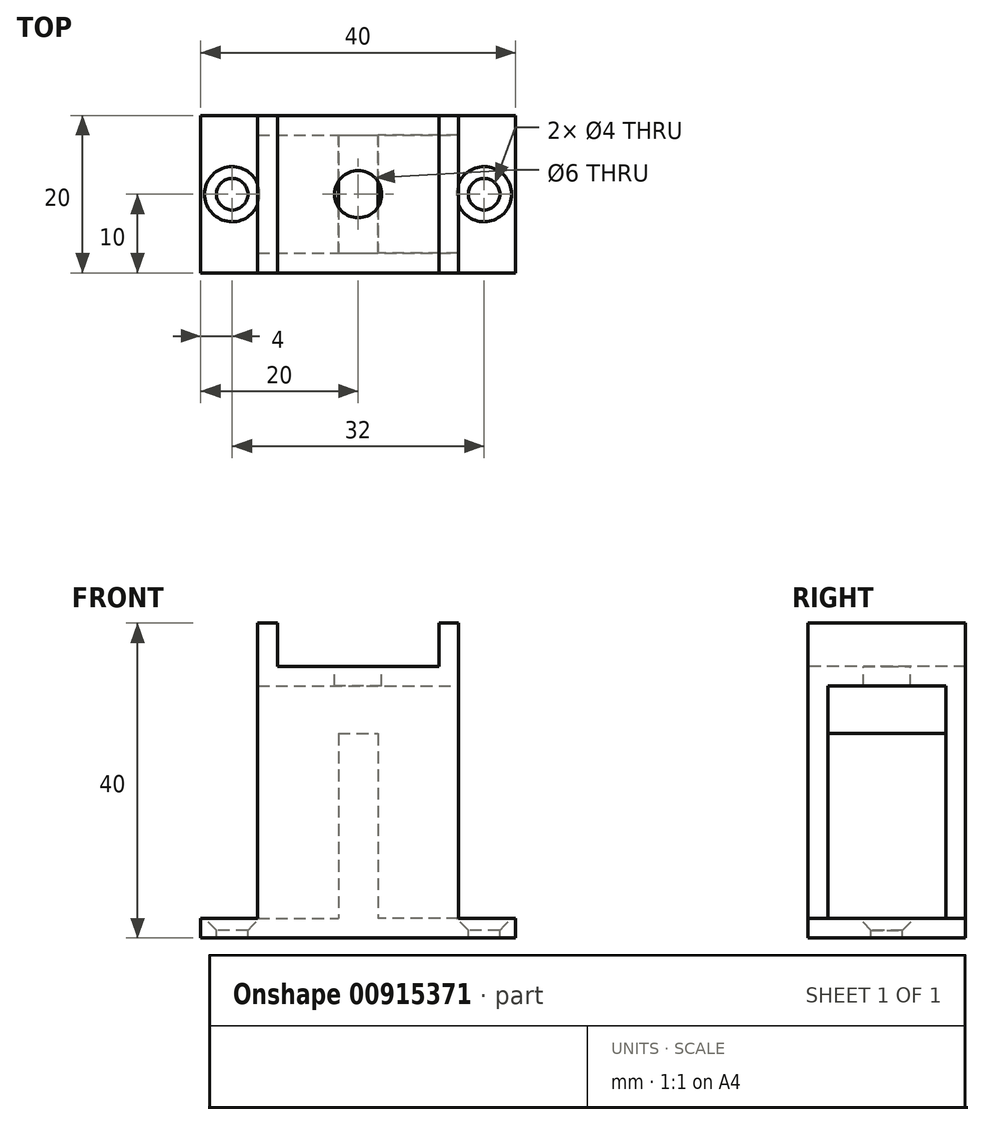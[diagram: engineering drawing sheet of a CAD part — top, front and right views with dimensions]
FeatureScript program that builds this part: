
annotation { "Feature Type Name" : "Feature", "Feature Type Description" : "" }
export const myFeature = defineFeature(function(context is Context, id is Id, definition is map)
    precondition{}
    {
        {
            var Q0;
            Q0=qCreatedBy(makeId("Top.planeOp"),FACE);
            var sketch = newSketch(context, id + "F0", { "sketchPlane" : qUnion([Q0])});
            skLineSegment(sketch, "E0.bottom", {"start": v(-20, 10) * mm, "end": v(20, 10) * mm});
            skLineSegment(sketch, "E0.top", {"start": v(-20, -10) * mm, "end": v(20, -10) * mm});
            skLineSegment(sketch, "E0.left", {"start": v(-20, 10) * mm, "end": v(-20, -10) * mm});
            skLineSegment(sketch, "E0.right", {"start": v(20, 10) * mm, "end": v(20, -10) * mm});
            skSolve(sketch);
        }
        {
            var Q0;
            Q0=makeQuery(id+"F0.imprint","IMPRINT",FACE,{"disambiguationData":[TD([[makeQuery(id+"F0.imprint","IMPRINT",EDGE,{"derivedFrom":sQuery(id+"F0.wireOp",EDGE,"E0.bottom")}),-1.0]])]});
            extrude(context, id + "F1", {"entities" : qUnion([Q0]), "depth" : 40 * mm, "offsetDistance" : 25 * mm});
        }
        {
            var Q0;
            Q0=qCreatedBy(makeId("Top.planeOp"),FACE);
            var sketch = newSketch(context, id + "F2", { "sketchPlane" : qUnion([Q0])});
            skLineSegment(sketch, "E1.bottom", {"start": v(-20, 7.5) * mm, "end": v(-2.5, 7.5) * mm});
            skLineSegment(sketch, "E1.top", {"start": v(-20, -7.5) * mm, "end": v(-2.5, -7.5) * mm});
            skLineSegment(sketch, "E1.left", {"start": v(-20, 7.5) * mm, "end": v(-20, -7.5) * mm});
            skLineSegment(sketch, "E1.right", {"start": v(-2.5, 7.5) * mm, "end": v(-2.5, -7.5) * mm});
            skLineSegment(sketch, "E2.MirrorCS", {"start": v(20, 7.5) * mm, "end": v(2.5, 7.5) * mm});
            skLineSegment(sketch, "E3.MirrorCS", {"start": v(2.5, 7.5) * mm, "end": v(2.5, -7.5) * mm});
            skLineSegment(sketch, "E4.MirrorCS", {"start": v(20, -7.5) * mm, "end": v(2.5, -7.5) * mm});
            skLineSegment(sketch, "E5.MirrorCS", {"start": v(20, 7.5) * mm, "end": v(20, -7.5) * mm});
            skSolve(sketch);
        }
        {
            var Q0;
            Q0 = qSketchRegion(id + "F2", true);
            extrude(context, id + "F3", {"entities" : qUnion([Q0]), "operationType" : NewBodyOperationType.REMOVE, "depth" : 32 * mm, "offsetDistance" : 25 * mm, "hasSecondDirection" : true, "secondDirectionOppositeDirection" : false, "secondDirectionDepth" : 2.5 * mm});
        }
        {
            var Q0;
            Q0=qCreatedBy(makeId("Front.planeOp"),FACE);
            var sketch = newSketch(context, id + "F4", { "sketchPlane" : qUnion([Q0])});
            skLineSegment(sketch, "E6.bottom", {"start": v(-10.25, 40) * mm, "end": v(10.25, 40) * mm});
            skLineSegment(sketch, "E6.top", {"start": v(-10.25, 34.5) * mm, "end": v(10.25, 34.5) * mm});
            skLineSegment(sketch, "E6.left", {"start": v(-10.25, 40) * mm, "end": v(-10.25, 34.5) * mm});
            skLineSegment(sketch, "E6.right", {"start": v(10.25, 40) * mm, "end": v(10.25, 34.5) * mm});
            skLineSegment(sketch, "E7.bottom", {"start": v(-20, 40) * mm, "end": v(-12.75, 40) * mm});
            skLineSegment(sketch, "E7.top", {"start": v(-20, 2.5) * mm, "end": v(-12.75, 2.5) * mm});
            skLineSegment(sketch, "E7.left", {"start": v(-20, 40) * mm, "end": v(-20, 2.5) * mm});
            skLineSegment(sketch, "E7.right", {"start": v(-12.75, 40) * mm, "end": v(-12.75, 2.5) * mm});
            skLineSegment(sketch, "E8.MirrorCS", {"start": v(12.75, 40) * mm, "end": v(12.75, 2.5) * mm});
            skLineSegment(sketch, "E9.MirrorCS", {"start": v(20, 40) * mm, "end": v(12.75, 40) * mm});
            skLineSegment(sketch, "E10.MirrorCS", {"start": v(20, 40) * mm, "end": v(20, 2.5) * mm});
            skLineSegment(sketch, "E11.MirrorCS", {"start": v(20, 2.5) * mm, "end": v(12.75, 2.5) * mm});
            skSolve(sketch);
        }
        {
            var Q0;
            Q0 = qSketchRegion(id + "F4", true);
            extrude(context, id + "F5", {"entities" : qUnion([Q0]), "operationType" : NewBodyOperationType.REMOVE, "oppositeDirection" : true, "depth" : 25 * mm, "offsetDistance" : 25 * mm, "hasSecondDirection" : true, "secondDirectionOppositeDirection" : false, "secondDirectionDepth" : 25 * mm});
        }
        {
            var Q0;
            Q0=qCreatedBy(makeId("Right.planeOp"),FACE);
            var sketch = newSketch(context, id + "F6", { "sketchPlane" : qUnion([Q0])});
            skLineSegment(sketch, "E12.bottom", {"start": v(-7.5, 32) * mm, "end": v(7.5, 32) * mm});
            skLineSegment(sketch, "E12.top", {"start": v(-7.5, 26) * mm, "end": v(7.5, 26) * mm});
            skLineSegment(sketch, "E12.left", {"start": v(-7.5, 32) * mm, "end": v(-7.5, 26) * mm});
            skLineSegment(sketch, "E12.right", {"start": v(7.5, 32) * mm, "end": v(7.5, 26) * mm});
            skSolve(sketch);
        }
        {
            var Q0;
            Q0 = qSketchRegion(id + "F6", true);
            extrude(context, id + "F7", {"entities" : qUnion([Q0]), "operationType" : NewBodyOperationType.REMOVE, "oppositeDirection" : true, "depth" : 25 * mm, "offsetDistance" : 25 * mm, "hasSecondDirection" : true, "secondDirectionOppositeDirection" : false, "secondDirectionDepth" : 25 * mm});
        }
        {
            var Q0;
            Q0=qCreatedBy(makeId("Top.planeOp"),FACE);
            var sketch = newSketch(context, id + "F8", { "sketchPlane" : qUnion([Q0])});
            skCircle(sketch, "E13", {"center": v(-16, 0) * mm, "radius": 2 * mm});
            skCircle(sketch, "E14.MirrorC", {"center": v(16, 0) * mm, "radius": 2 * mm});
            skSolve(sketch);
        }
        {
            var Q0;
            Q0 = qSketchRegion(id + "F8", true);
            extrude(context, id + "F9", {"entities" : qUnion([Q0]), "operationType" : NewBodyOperationType.REMOVE, "oppositeDirection" : true, "depth" : 25 * mm, "offsetDistance" : 25 * mm, "hasSecondDirection" : true, "secondDirectionOppositeDirection" : false, "secondDirectionDepth" : 25 * mm});
        }
        {
            var Q0;
            Q0=makeQuery(id+"F9.boolean.opBoolean","INTERSECT",EDGE,{"derivedFrom":[makeQuery(id+"F5.boolean.opBoolean","MERGE",FACE,{"derivedFrom":[makeQuery(id+"F3.boolean.opBoolean","COPY",FACE,{"derivedFrom":makeQuery(id+"F3.opExtrude","CAP_FACE",FACE,{"disambiguationData":[OSD([sQuery(id+"F2.wireOp",EDGE,"E1.bottom"),sQuery(id+"F2.wireOp",EDGE,"E1.top"),sQuery(id+"F2.wireOp",EDGE,"E1.left"),sQuery(id+"F2.wireOp",EDGE,"E1.right")])],"isStart":true})})],"fromTools":[makeQuery(id+"F5.opExtrude","SWEPT_FACE",FACE,{"disambiguationData":[OSD([sQuery(id+"F4.wireOp",EDGE,"E7.top")])]})]}),makeQuery(id+"F9.opExtrude","SWEPT_FACE",FACE,{"disambiguationData":[OSD([sQuery(id+"F8.wireOp",EDGE,"E13")])]})]});
            var Q1;
            Q1=makeQuery(id+"F9.boolean.opBoolean","INTERSECT",EDGE,{"derivedFrom":[makeQuery(id+"F5.boolean.opBoolean","MERGE",FACE,{"derivedFrom":[makeQuery(id+"F3.boolean.opBoolean","COPY",FACE,{"derivedFrom":makeQuery(id+"F3.opExtrude","CAP_FACE",FACE,{"disambiguationData":[OSD([sQuery(id+"F2.wireOp",EDGE,"E2.MirrorCS"),sQuery(id+"F2.wireOp",EDGE,"E3.MirrorCS"),sQuery(id+"F2.wireOp",EDGE,"E4.MirrorCS"),sQuery(id+"F2.wireOp",EDGE,"E5.MirrorCS")])],"isStart":true})})],"fromTools":[makeQuery(id+"F5.opExtrude","SWEPT_FACE",FACE,{"disambiguationData":[OSD([sQuery(id+"F4.wireOp",EDGE,"E11.MirrorCS")])]})]}),makeQuery(id+"F9.opExtrude","SWEPT_FACE",FACE,{"disambiguationData":[OSD([sQuery(id+"F8.wireOp",EDGE,"E14.MirrorC")])]})]});
            chamfer(context, id + "F10", {"entities" : qUnion([Q0, Q1]), "width" : 1.5 * mm, "tangentPropagation" : true});
        }
        {
            var Q0;
            Q0=makeQuery(id+"F5.boolean.opBoolean","COPY",FACE,{"derivedFrom":makeQuery(id+"F5.opExtrude","SWEPT_FACE",FACE,{"disambiguationData":[OSD([sQuery(id+"F4.wireOp",EDGE,"E6.top")])]})});
            cPlane(context, id + "F11", {"entities" : qUnion([Q0]), "cplaneType" : CPlaneType.OFFSET, "offset" : 0 * mm, "width" : 150 * mm, "height" : 150 * mm});
        }
        {
            var Q0;
            Q0=qCreatedBy(id+"F11.planeOp",FACE);
            var sketch = newSketch(context, id + "F12", { "sketchPlane" : qUnion([Q0])});
            skCircle(sketch, "E15", {"center": v(0, 0) * mm, "radius": 3 * mm});
            skSolve(sketch);
        }
        {
            var Q0;
            Q0 = qSketchRegion(id + "F12", true);
            extrude(context, id + "F13", {"entities" : qUnion([Q0]), "operationType" : NewBodyOperationType.REMOVE, "oppositeDirection" : true, "depth" : 3 * mm, "offsetDistance" : 25 * mm});
        }
    });
